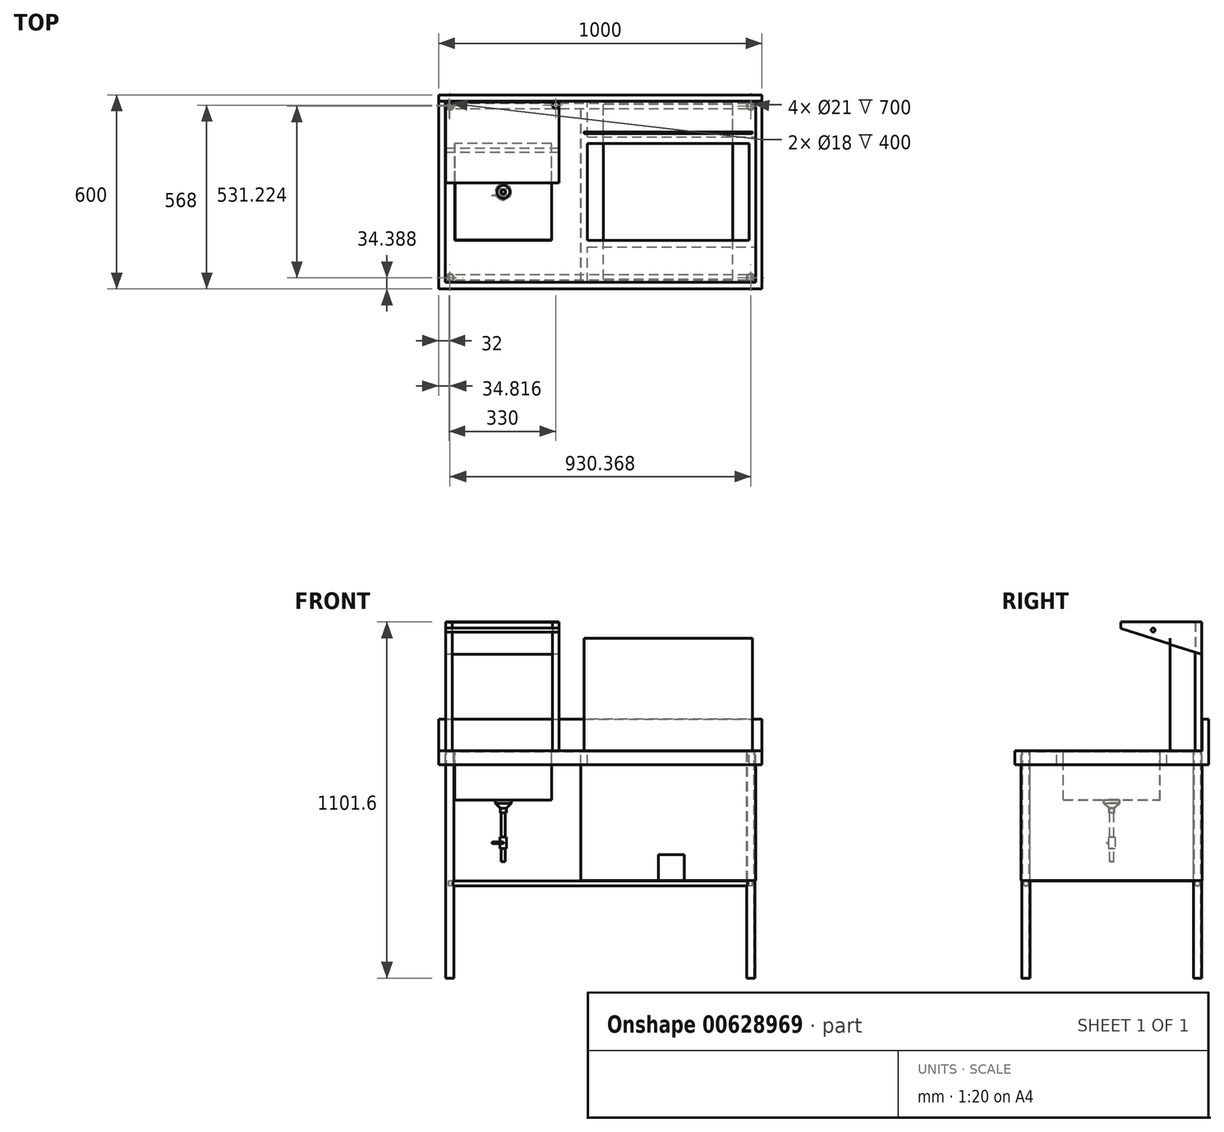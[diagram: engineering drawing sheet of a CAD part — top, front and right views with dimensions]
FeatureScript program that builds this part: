
annotation { "Feature Type Name" : "Feature", "Feature Type Description" : "" }
export const myFeature = defineFeature(function(context is Context, id is Id, definition is map)
    precondition{}
    {
        {
            var Q0;
            Q0=qCreatedBy(makeId("Top.planeOp"),FACE);
            var sketch = newSketch(context, id + "F0", { "sketchPlane" : qUnion([Q0])});
            skPoint(sketch, "E0.middle", {"position": v(230, 0) * mm});
            skLineSegment(sketch, "E1.bottom", {"start": v(500, -300) * mm, "end": v(-500, -300) * mm});
            skLineSegment(sketch, "E1.top", {"start": v(500, 300) * mm, "end": v(-500, 300) * mm});
            skLineSegment(sketch, "E1.left", {"start": v(500, -300) * mm, "end": v(500, 300) * mm});
            skLineSegment(sketch, "E1.right", {"start": v(-500, -300) * mm, "end": v(-500, 300) * mm});
            skPoint(sketch, "E1.middle", {"position": v(0, 0) * mm});
            skSolve(sketch);
        }
        {
            var Q0;
            Q0 = qSketchRegion(id + "F0", true);
            extrude(context, id + "F1", {"entities" : qUnion([Q0]), "oppositeDirection" : true, "depth" : 40 * mm, "offsetDistance" : 25 * mm});
        }
        {
            var Q0;
            Q0=makeQuery(id+"F1.opExtrude","CAP_FACE",FACE,{"disambiguationData":[OSD([sQuery(id+"F0.wireOp",EDGE,"E1.bottom"),sQuery(id+"F0.wireOp",EDGE,"E1.top"),sQuery(id+"F0.wireOp",EDGE,"E1.left"),sQuery(id+"F0.wireOp",EDGE,"E1.right")])],"isStart":false});
            shell(context, id + "F2", {"entities" : qUnion([Q0]), "thickness" : 0.8 * mm});
        }
        {
            var Q0;
            Q0=qCreatedBy(makeId("Top.planeOp"),FACE);
            var sketch = newSketch(context, id + "F3", { "sketchPlane" : qUnion([Q0])});
            skLineSegment(sketch, "E2.bottom", {"start": v(460, -150) * mm, "end": v(-40, -150) * mm});
            skLineSegment(sketch, "E2.top", {"start": v(460, 150) * mm, "end": v(-40, 150) * mm});
            skLineSegment(sketch, "E2.left", {"start": v(460, -150) * mm, "end": v(460, 150) * mm});
            skLineSegment(sketch, "E2.right", {"start": v(-40, -150) * mm, "end": v(-40, 150) * mm});
            skPoint(sketch, "E2.middle", {"position": v(210, 0) * mm});
            skLineSegment(sketch, "E3.bottom", {"start": v(-150, -150) * mm, "end": v(-450, -150) * mm});
            skLineSegment(sketch, "E3.top", {"start": v(-150, 150) * mm, "end": v(-450, 150) * mm});
            skLineSegment(sketch, "E3.left", {"start": v(-150, -150) * mm, "end": v(-150, 150) * mm});
            skLineSegment(sketch, "E3.right", {"start": v(-450, -150) * mm, "end": v(-450, 150) * mm});
            skPoint(sketch, "E3.middle", {"position": v(-300, 0) * mm});
            skPoint(sketch, "E3.middle.positionSnap0", {"position": v(-40, 0) * mm});
            skPoint(sketch, "E3.centerSnap0", {"position": v(-40, 0) * mm});
            skSolve(sketch);
        }
        {
            var Q0;
            Q0 = qSketchRegion(id + "F3", true);
            extrude(context, id + "F4", {"entities" : qUnion([Q0]), "operationType" : NewBodyOperationType.REMOVE, "endBound" : BoundingType.THROUGH_ALL, "oppositeDirection" : true, "depth" : 25 * mm, "offsetDistance" : 25 * mm});
        }
        {
            var Q0;
            Q0=qCreatedBy(makeId("Top.planeOp"),FACE);
            var sketch = newSketch(context, id + "F5", { "sketchPlane" : qUnion([Q0])});
            skLineSegment(sketch, "E4.bottom", {"start": v(-150, -150) * mm, "end": v(-450, -150) * mm});
            skLineSegment(sketch, "E4.top", {"start": v(-150, 150) * mm, "end": v(-450, 150) * mm});
            skLineSegment(sketch, "E4.left", {"start": v(-150, -150) * mm, "end": v(-150, 150) * mm});
            skLineSegment(sketch, "E4.right", {"start": v(-450, -150) * mm, "end": v(-450, 150) * mm});
            skPoint(sketch, "E4.middle", {"position": v(-300, 0) * mm});
            skSolve(sketch);
        }
        {
            var Q0;
            Q0 = qSketchRegion(id + "F5", true);
            extrude(context, id + "F6", {"entities" : qUnion([Q0]), "oppositeDirection" : true, "depth" : 150 * mm, "offsetDistance" : 25 * mm});
        }
        {
            var Q0;
            Q0=makeQuery(id+"F6.opExtrude","CAP_FACE",FACE,{"disambiguationData":[OSD([sQuery(id+"F5.wireOp",EDGE,"E4.bottom"),sQuery(id+"F5.wireOp",EDGE,"E4.top"),sQuery(id+"F5.wireOp",EDGE,"E4.left"),sQuery(id+"F5.wireOp",EDGE,"E4.right")])],"isStart":true});
            shell(context, id + "F7", {"entities" : qUnion([Q0]), "thickness" : 0.8 * mm});
        }
        {
            var Q0;
            Q0=makeQuery(id+"F7.opShell","OFFSET_FACE",FACE,{"disambiguationData":[OSD([sQuery(id+"F5.wireOp",EDGE,"E4.bottom"),sQuery(id+"F5.wireOp",EDGE,"E4.top"),sQuery(id+"F5.wireOp",EDGE,"E4.left"),sQuery(id+"F5.wireOp",EDGE,"E4.right")])]});
            var sketch = newSketch(context, id + "F8", { "sketchPlane" : qUnion([Q0])});
            skPoint(sketch, "E5.center", {"position": v(-300, 0) * mm});
            skCircle(sketch, "E6", {"center": v(-300, 0) * mm, "radius": 20 * mm});
            skSolve(sketch);
        }
        {
            var Q0;
            Q0 = qSketchRegion(id + "F8", true);
            extrude(context, id + "F9", {"entities" : qUnion([Q0]), "operationType" : NewBodyOperationType.REMOVE, "endBound" : BoundingType.UP_TO_NEXT, "oppositeDirection" : true, "depth" : 25 * mm, "offsetDistance" : 25 * mm});
        }
        {
            var Q0;
            Q0=makeQuery(id+"F2.opShell","OFFSET_FACE",FACE,{"disambiguationData":[OSD([sQuery(id+"F0.wireOp",EDGE,"E1.bottom"),sQuery(id+"F0.wireOp",EDGE,"E1.top"),sQuery(id+"F0.wireOp",EDGE,"E1.left"),sQuery(id+"F0.wireOp",EDGE,"E1.right")])]});
            var sketch = newSketch(context, id + "F10", { "sketchPlane" : qUnion([Q0])});
            skLineSegment(sketch, "E7.bottom", {"start": v(500, 300) * mm, "end": v(-500, 300) * mm});
            skLineSegment(sketch, "E7.top", {"start": v(500, -300) * mm, "end": v(-500, -300) * mm});
            skLineSegment(sketch, "E7.left", {"start": v(500, 300) * mm, "end": v(500, -300) * mm});
            skLineSegment(sketch, "E7.right", {"start": v(-500, 300) * mm, "end": v(-500, -300) * mm});
            skPoint(sketch, "E7.middle", {"position": v(0, 0) * mm});
            skLineSegment(sketch, "E8.0", {"start": v(480, 280) * mm, "end": v(-40, 280) * mm});
            skLineSegment(sketch, "E8.1", {"start": v(480, 280) * mm, "end": v(480, 170) * mm});
            skLineSegment(sketch, "E8.2", {"start": v(480, -280) * mm, "end": v(-40, -280) * mm});
            skLineSegment(sketch, "E8.3", {"start": v(-480, 280) * mm, "end": v(-480, -280) * mm});
            skLineSegment(sketch, "E9.left", {"start": v(-40, 280) * mm, "end": v(-40, 170) * mm});
            skLineSegment(sketch, "E9.right", {"start": v(-60, 280) * mm, "end": v(-60, -280) * mm});
            skLineSegment(sketch, "E10.trimOffspring", {"start": v(-60, 280) * mm, "end": v(-480, 280) * mm});
            skLineSegment(sketch, "E11.trimOffspring", {"start": v(-60, -280) * mm, "end": v(-480, -280) * mm});
            skLineSegment(sketch, "E12.bottom", {"start": v(-40, 150) * mm, "end": v(460, 150) * mm});
            skLineSegment(sketch, "E12.top", {"start": v(-40, 170) * mm, "end": v(480, 170) * mm});
            skLineSegment(sketch, "E13.trimOffspring", {"start": v(-40, 150) * mm, "end": v(-40, -150) * mm});
            skLineSegment(sketch, "E14.bottom", {"start": v(-40, -150) * mm, "end": v(460, -150) * mm});
            skLineSegment(sketch, "E14.top", {"start": v(-40, -170) * mm, "end": v(480, -170) * mm});
            skLineSegment(sketch, "E15.trimOffspring", {"start": v(-40, -170) * mm, "end": v(-40, -280) * mm});
            skLineSegment(sketch, "E16.trimOffspring", {"start": v(480, -170) * mm, "end": v(480, -280) * mm});
            skLineSegment(sketch, "E17", {"start": v(460, 150) * mm, "end": v(460, -150) * mm});
            skSolve(sketch);
        }
        {
            var Q0;
            Q0 = qSketchRegion(id + "F10", true);
            extrude(context, id + "F11", {"entities" : qUnion([Q0]), "operationType" : NewBodyOperationType.ADD, "depth" : 40 * mm, "offsetDistance" : 25 * mm});
        }
        {
            var Q0;
            Q0=makeQuery(id+"F11.boolean.opBoolean","SPLIT",FACE,{"disambiguationData":[TD([makeQuery(id+"F4.boolean.opBoolean","COPY",FACE,{"derivedFrom":makeQuery(id+"F4.opExtrude","SWEPT_FACE",FACE,{"disambiguationData":[OSD([sQuery(id+"F3.wireOp",EDGE,"E3.bottom")])]})})])],"derivedFrom":makeQuery(id+"F2.opShell","OFFSET_FACE",FACE,{"disambiguationData":[OSD([sQuery(id+"F0.wireOp",EDGE,"E1.bottom"),sQuery(id+"F0.wireOp",EDGE,"E1.top"),sQuery(id+"F0.wireOp",EDGE,"E1.left"),sQuery(id+"F0.wireOp",EDGE,"E1.right")])]})});
            var sketch = newSketch(context, id + "F12", { "sketchPlane" : qUnion([Q0])});
            skCircle(sketch, "E18", {"center": v(-465.18, 265.61) * mm, "radius": 12.5 * mm});
            skCircle(sketch, "E19.0", {"center": v(-465.18, 265.61) * mm, "radius": 10.5 * mm});
            skLineSegment(sketch, "E20", {"start": v(0, 0) * mm, "end": v(0, 330.65) * mm, "construction": true});
            skLineSegment(sketch, "E21", {"start": v(0, 0) * mm, "end": v(239.47, 0) * mm, "construction": true});
            skLineSegment(sketch, "E22.MirrorCS", {"start": v(0, 0) * mm, "end": v(0, -330.65) * mm, "construction": true});
            skCircle(sketch, "E23.MirrorC", {"center": v(-465.18, -265.61) * mm, "radius": 12.5 * mm});
            skCircle(sketch, "E24.MirrorC", {"center": v(465.18, 265.61) * mm, "radius": 12.5 * mm});
            skCircle(sketch, "E25.MirrorC", {"center": v(465.18, 265.61) * mm, "radius": 10.5 * mm});
            skCircle(sketch, "E26.MirrorC", {"center": v(465.18, -265.61) * mm, "radius": 12.5 * mm});
            skCircle(sketch, "E27.MirrorC", {"center": v(-465.18, -265.61) * mm, "radius": 10.5 * mm});
            skCircle(sketch, "E28.MirrorC", {"center": v(465.18, -265.61) * mm, "radius": 10.5 * mm});
            skSolve(sketch);
        }
        {
            var Q0;
            Q0 = qSketchRegion(id + "F12", true);
            extrude(context, id + "F13", {"entities" : qUnion([Q0]), "operationType" : NewBodyOperationType.ADD, "depth" : 700 * mm, "offsetDistance" : 25 * mm});
        }
        {
            var Q0;
            Q0=qCreatedBy(makeId("Top.planeOp"),FACE);
            cPlane(context, id + "F14", {"entities" : qUnion([Q0]), "cplaneType" : CPlaneType.OFFSET, "offset" : 1.2 * mm, "width" : 150 * mm, "height" : 150 * mm});
        }
        {
            var Q0;
            Q0=qCreatedBy(makeId("Top.planeOp"),FACE);
            cPlane(context, id + "F15", {"entities" : qUnion([Q0]), "cplaneType" : CPlaneType.OFFSET, "offset" : 400 * mm, "oppositeDirection" : true, "width" : 150 * mm, "height" : 150 * mm});
        }
        {
            var Q0;
            Q0=qCreatedBy(makeId("Right.planeOp"),FACE);
            var sketch = newSketch(context, id + "F16", { "sketchPlane" : qUnion([Q0])});
            skCircle(sketch, "E29", {"center": v(265, -408) * mm, "radius": 8 * mm});
            skCircle(sketch, "E30", {"center": v(-265, -408) * mm, "radius": 8 * mm});
            skSolve(sketch);
        }
        {
            var Q0;
            Q0 = qSketchRegion(id + "F16", true);
            extrude(context, id + "F17", {"entities" : qUnion([Q0]), "operationType" : NewBodyOperationType.ADD, "depth" : 940 * mm, "offsetDistance" : 25 * mm, "symmetric" : true});
        }
        {
            var Q0;
            Q0=qCreatedBy(id+"F15.planeOp",FACE);
            var sketch = newSketch(context, id + "F18", { "sketchPlane" : qUnion([Q0])});
            skLineSegment(sketch, "E31.bottom", {"start": v(410, -270) * mm, "end": v(10, -270) * mm});
            skLineSegment(sketch, "E31.top", {"start": v(410, 270) * mm, "end": v(10, 270) * mm});
            skLineSegment(sketch, "E31.left", {"start": v(410, -270) * mm, "end": v(410, 270) * mm});
            skLineSegment(sketch, "E31.right", {"start": v(10, -270) * mm, "end": v(10, 270) * mm});
            skPoint(sketch, "E31.middle", {"position": v(210, 0) * mm});
            skSolve(sketch);
        }
        {
            var Q0;
            Q0 = qSketchRegion(id + "F18", true);
            extrude(context, id + "F19", {"entities" : qUnion([Q0]), "operationType" : NewBodyOperationType.ADD, "depth" : 1 * mm, "offsetDistance" : 25 * mm});
        }
        {
            var Q0;
            Q0=makeQuery(id+"F1.opExtrude","CAP_FACE",FACE,{"disambiguationData":[OSD([sQuery(id+"F0.wireOp",EDGE,"E1.bottom"),sQuery(id+"F0.wireOp",EDGE,"E1.top"),sQuery(id+"F0.wireOp",EDGE,"E1.left"),sQuery(id+"F0.wireOp",EDGE,"E1.right")])],"isStart":true});
            var sketch = newSketch(context, id + "F20", { "sketchPlane" : qUnion([Q0])});
            skLineSegment(sketch, "E32.bottom", {"start": v(-50, 181) * mm, "end": v(470, 181) * mm});
            skLineSegment(sketch, "E32.top", {"start": v(-50, 180) * mm, "end": v(470, 180) * mm});
            skLineSegment(sketch, "E32.left", {"start": v(-50, 181) * mm, "end": v(-50, 180) * mm});
            skLineSegment(sketch, "E32.right", {"start": v(470, 181) * mm, "end": v(470, 180) * mm});
            skSolve(sketch);
        }
        {
            var Q0;
            Q0 = qSketchRegion(id + "F20", true);
            extrude(context, id + "F21", {"entities" : qUnion([Q0]), "operationType" : NewBodyOperationType.ADD, "depth" : 350 * mm, "offsetDistance" : 25 * mm});
        }
        {
            var Q0;
            Q0=makeQuery(id+"F21.opExtrude","SWEPT_FACE",FACE,{"disambiguationData":[OSD([sQuery(id+"F20.wireOp",EDGE,"E32.right")])]});
            var sketch = newSketch(context, id + "F22", { "sketchPlane" : qUnion([Q0])});
            skCircle(sketch, "E33", {"center": v(183.5, 2.5) * mm, "radius": 2.5 * mm});
            skSolve(sketch);
        }
        {
            var Q0;
            Q0 = qSketchRegion(id + "F22", true);
            var Q1;
            Q1=makeQuery(id+"F21.opExtrude","SWEPT_FACE",FACE,{"disambiguationData":[OSD([sQuery(id+"F20.wireOp",EDGE,"E32.left")])]});
            extrude(context, id + "F23", {"entities" : qUnion([Q0]), "operationType" : NewBodyOperationType.ADD, "endBound" : BoundingType.UP_TO_SURFACE, "oppositeDirection" : true, "depth" : 500 * mm, "endBoundEntityFace" : qUnion([Q1]), "offsetDistance" : 25 * mm});
        }
        {
            var Q0;
            Q0=makeQuery(id+"F11.opExtrude","CAP_FACE",FACE,{"disambiguationData":[OSD([sQuery(id+"F10.wireOp",EDGE,"E7.bottom"),sQuery(id+"F10.wireOp",EDGE,"E7.top"),sQuery(id+"F10.wireOp",EDGE,"E7.left"),sQuery(id+"F10.wireOp",EDGE,"E7.right"),sQuery(id+"F10.wireOp",EDGE,"E8.0"),sQuery(id+"F10.wireOp",EDGE,"E8.1"),sQuery(id+"F10.wireOp",EDGE,"E8.2"),sQuery(id+"F10.wireOp",EDGE,"E8.3"),sQuery(id+"F10.wireOp",EDGE,"E9.left"),sQuery(id+"F10.wireOp",EDGE,"E9.right"),sQuery(id+"F10.wireOp",EDGE,"E10.trimOffspring"),sQuery(id+"F10.wireOp",EDGE,"E11.trimOffspring"),sQuery(id+"F10.wireOp",EDGE,"E12.bottom"),sQuery(id+"F10.wireOp",EDGE,"E12.top"),sQuery(id+"F10.wireOp",EDGE,"E13.trimOffspring"),sQuery(id+"F10.wireOp",EDGE,"192a2169-85b4-4757-ab78-00c488c10352.trimOffspring"),sQuery(id+"F10.wireOp",EDGE,"E14.bottom"),sQuery(id+"F10.wireOp",EDGE,"E14.top"),sQuery(id+"F10.wireOp",EDGE,"E15.trimOffspring"),sQuery(id+"F10.wireOp",EDGE,"E16.trimOffspring")])],"isStart":false});
            var sketch = newSketch(context, id + "F24", { "sketchPlane" : qUnion([Q0])});
            skLineSegment(sketch, "E34.bottom", {"start": v(-60, 280) * mm, "end": v(480, 280) * mm});
            skLineSegment(sketch, "E34.top", {"start": v(-60, -280) * mm, "end": v(480, -280) * mm});
            skLineSegment(sketch, "E34.left", {"start": v(-60, 280) * mm, "end": v(-60, -280) * mm});
            skLineSegment(sketch, "E34.right", {"start": v(480, 280) * mm, "end": v(480, -280) * mm});
            skSolve(sketch);
        }
        {
            var Q0;
            Q0 = qSketchRegion(id + "F24", true);
            var Q1;
            Q1=makeQuery(id+"F19.opExtrude","CAP_FACE",FACE,{"disambiguationData":[OSD([sQuery(id+"F18.wireOp",EDGE,"E31.bottom"),sQuery(id+"F18.wireOp",EDGE,"E31.top"),sQuery(id+"F18.wireOp",EDGE,"E31.left"),sQuery(id+"F18.wireOp",EDGE,"E31.right")])],"isStart":false});
            extrude(context, id + "F25", {"entities" : qUnion([Q0]), "endBound" : BoundingType.UP_TO_SURFACE, "depth" : 25 * mm, "endBoundEntityFace" : qUnion([Q1]), "offsetDistance" : 25 * mm});
        }
        {
            var Q0;
            Q0=makeQuery(id+"F25.opExtrude","CAP_FACE",FACE,{"disambiguationData":[OSD([sQuery(id+"F24.wireOp",EDGE,"E34.bottom"),sQuery(id+"F24.wireOp",EDGE,"E34.top"),sQuery(id+"F24.wireOp",EDGE,"E34.left"),sQuery(id+"F24.wireOp",EDGE,"E34.right")])],"isStart":true});
            var Q1;
            Q1=makeQuery(id+"F25.opExtrude","CAP_FACE",FACE,{"disambiguationData":[OSD([sQuery(id+"F24.wireOp",EDGE,"E34.bottom"),sQuery(id+"F24.wireOp",EDGE,"E34.top"),sQuery(id+"F24.wireOp",EDGE,"E34.left"),sQuery(id+"F24.wireOp",EDGE,"E34.right")])],"isStart":false});
            shell(context, id + "F26", {"entities" : qUnion([Q0, Q1]), "thickness" : 0.8 * mm});
        }
        {
            var Q0;
            Q0=makeQuery(id+"F25.opExtrude","SWEPT_FACE",FACE,{"disambiguationData":[OSD([sQuery(id+"F24.wireOp",EDGE,"E34.bottom")])]});
            var sketch = newSketch(context, id + "F27", { "sketchPlane" : qUnion([Q0])});
            skLineSegment(sketch, "E35.bottom", {"start": v(180, -399) * mm, "end": v(260, -399) * mm});
            skLineSegment(sketch, "E35.top", {"start": v(180, -319) * mm, "end": v(260, -319) * mm});
            skLineSegment(sketch, "E35.left", {"start": v(180, -399) * mm, "end": v(180, -319) * mm});
            skLineSegment(sketch, "E35.right", {"start": v(260, -399) * mm, "end": v(260, -319) * mm});
            skSolve(sketch);
        }
        {
            var Q0;
            Q0 = qSketchRegion(id + "F27", true);
            extrude(context, id + "F28", {"entities" : qUnion([Q0]), "operationType" : NewBodyOperationType.REMOVE, "oppositeDirection" : true, "depth" : 25 * mm, "offsetDistance" : 25 * mm});
        }
        {
            var Q0;
            Q0=qCreatedBy(makeId("Front.planeOp"),FACE);
            var sketch = newSketch(context, id + "F29", { "sketchPlane" : qUnion([Q0])});
            skLineSegment(sketch, "E36", {"start": v(-300, -110.82) * mm, "end": v(-300, -187.74) * mm, "construction": true});
            skLineSegment(sketch, "E37", {"start": v(-325, -150) * mm, "end": v(-325, -160) * mm});
            skLineSegment(sketch, "E38", {"start": v(-325, -160) * mm, "end": v(-309.25, -175.75) * mm});
            skLineSegment(sketch, "E39", {"start": v(-309.25, -175.75) * mm, "end": v(-309.25, -190) * mm});
            skLineSegment(sketch, "E40", {"start": v(-325, -150) * mm, "end": v(-300, -150) * mm});
            skLineSegment(sketch, "E41", {"start": v(-309.25, -190) * mm, "end": v(-300, -190) * mm});
            skLineSegment(sketch, "E42", {"start": v(-300, -150) * mm, "end": v(-300, -190) * mm});
            skSolve(sketch);
        }
        {
            var Q0;
            Q0 = qSketchRegion(id + "F29", true);
            var Q1;
            Q1=sQuery(id+"F29.wireOp",EDGE,"E36");
            revolve(context, id + "F30", {"operationType" : NewBodyOperationType.ADD, "entities" : qUnion([Q0]), "axis" : qUnion([Q1]), "revolveType" : RevolveType.FULL});
        }
        {
            var Q0;
            Q0=makeQuery(id+"F30.opRevolve","SWEPT_FACE",FACE,{"disambiguationData":[OSD([sQuery(id+"F29.wireOp",EDGE,"E41")])]});
            var Q1;
            Q1=makeQuery(id+"F30.opRevolve","SWEPT_FACE",FACE,{"disambiguationData":[OSD([sQuery(id+"F29.wireOp",EDGE,"E40")])]});
            shell(context, id + "F31", {"entities" : qUnion([Q0, Q1]), "thickness" : 2.5 * mm});
        }
        {
            var Q0;
            Q0=makeQuery(id+"F1.opExtrude","CAP_FACE",FACE,{"disambiguationData":[OSD([sQuery(id+"F0.wireOp",EDGE,"E1.bottom"),sQuery(id+"F0.wireOp",EDGE,"E1.top"),sQuery(id+"F0.wireOp",EDGE,"E1.left"),sQuery(id+"F0.wireOp",EDGE,"E1.right")])],"isStart":true});
            var sketch = newSketch(context, id + "F32", { "sketchPlane" : qUnion([Q0])});
            skLineSegment(sketch, "E43.top", {"start": v(500, -300) * mm, "end": v(-500, -300) * mm});
            skLineSegment(sketch, "E43.left", {"start": v(500, 280) * mm, "end": v(500, -300) * mm});
            skLineSegment(sketch, "E43.right", {"start": v(-500, 280) * mm, "end": v(-500, -300) * mm});
            skPoint(sketch, "E43.middle", {"position": v(0, 0) * mm});
            skLineSegment(sketch, "E44.0", {"start": v(480, -280) * mm, "end": v(480, 280) * mm});
            skLineSegment(sketch, "E44.1", {"start": v(-480, -280) * mm, "end": v(480, -280) * mm});
            skLineSegment(sketch, "E44.2", {"start": v(-480, 280) * mm, "end": v(-480, -280) * mm});
            skLineSegment(sketch, "E44.3", {"start": v(500, 280) * mm, "end": v(480, 280) * mm});
            skLineSegment(sketch, "E45.trimOffspring", {"start": v(-480, 280) * mm, "end": v(-500, 280) * mm});
            skSolve(sketch);
        }
        {
            var Q0;
            Q0 = qSketchRegion(id + "F32", true);
            extrude(context, id + "F33", {"entities" : qUnion([Q0]), "depth" : 2 * mm, "offsetDistance" : 25 * mm});
        }
        {
            var Q0;
            Q0=makeQuery(id+"F1.opExtrude","CAP_FACE",FACE,{"disambiguationData":[OSD([sQuery(id+"F0.wireOp",EDGE,"E1.bottom"),sQuery(id+"F0.wireOp",EDGE,"E1.top"),sQuery(id+"F0.wireOp",EDGE,"E1.left"),sQuery(id+"F0.wireOp",EDGE,"E1.right")])],"isStart":true});
            var sketch = newSketch(context, id + "F34", { "sketchPlane" : qUnion([Q0])});
            skLineSegment(sketch, "E46.bottom", {"start": v(-500, 300) * mm, "end": v(500, 300) * mm});
            skLineSegment(sketch, "E46.top", {"start": v(-500, 280) * mm, "end": v(500, 280) * mm});
            skLineSegment(sketch, "E46.left", {"start": v(-500, 300) * mm, "end": v(-500, 280) * mm});
            skLineSegment(sketch, "E46.right", {"start": v(500, 300) * mm, "end": v(500, 280) * mm});
            skSolve(sketch);
        }
        {
            var Q0;
            Q0 = qSketchRegion(id + "F34", true);
            extrude(context, id + "F35", {"entities" : qUnion([Q0]), "operationType" : NewBodyOperationType.ADD, "depth" : 100 * mm, "offsetDistance" : 25 * mm});
        }
        {
            var Q0;
            Q0=qCreatedBy(makeId("Front.planeOp"),FACE);
            var sketch = newSketch(context, id + "F36", { "sketchPlane" : qUnion([Q0])});
            skLineSegment(sketch, "E47.bottom", {"start": v(-300, -190) * mm, "end": v(-306.35, -190) * mm});
            skLineSegment(sketch, "E47.top", {"start": v(-300, -340) * mm, "end": v(-306.35, -340) * mm});
            skLineSegment(sketch, "E47.left", {"start": v(-300, -190) * mm, "end": v(-300, -340) * mm});
            skLineSegment(sketch, "E47.right", {"start": v(-306.35, -190) * mm, "end": v(-306.35, -340) * mm});
            skSolve(sketch);
        }
        {
            var Q0;
            Q0=makeQuery(id+"F36.imprint","IMPRINT",FACE,{"disambiguationData":[TD([[makeQuery(id+"F36.imprint","IMPRINT",EDGE,{"derivedFrom":sQuery(id+"F36.wireOp",EDGE,"E47.bottom")}),1.0]])]});
            var Q1;
            Q1=sQuery(id+"F36.wireOp",EDGE,"E47.left");
            revolve(context, id + "F37", {"operationType" : NewBodyOperationType.ADD, "entities" : qUnion([Q0]), "axis" : qUnion([Q1]), "revolveType" : RevolveType.FULL});
        }
        {
            var Q0;
            Q0=qCreatedBy(makeId("Front.planeOp"),FACE);
            var sketch = newSketch(context, id + "F38", { "sketchPlane" : qUnion([Q0])});
            skLineSegment(sketch, "E48.bottom", {"start": v(-310.18, -265) * mm, "end": v(-290.18, -265) * mm});
            skLineSegment(sketch, "E48.top", {"start": v(-310.18, -300) * mm, "end": v(-290.18, -300) * mm});
            skLineSegment(sketch, "E48.left", {"start": v(-310.18, -265) * mm, "end": v(-310.18, -300) * mm});
            skLineSegment(sketch, "E48.right", {"start": v(-290.18, -265) * mm, "end": v(-290.18, -300) * mm});
            skSolve(sketch);
        }
        {
            var Q0;
            Q0 = qSketchRegion(id + "F38", true);
            extrude(context, id + "F39", {"entities" : qUnion([Q0]), "operationType" : NewBodyOperationType.ADD, "depth" : 20 * mm, "offsetDistance" : 25 * mm, "symmetric" : true});
        }
        {
            var Q0;
            Q0=makeQuery(id+"F39.opExtrude","CAP_FACE",FACE,{"disambiguationData":[OSD([sQuery(id+"F38.wireOp",EDGE,"E48.bottom"),sQuery(id+"F38.wireOp",EDGE,"E48.top"),sQuery(id+"F38.wireOp",EDGE,"E48.left"),sQuery(id+"F38.wireOp",EDGE,"E48.right")])],"isStart":false});
            var sketch = newSketch(context, id + "F40", { "sketchPlane" : qUnion([Q0])});
            skLineSegment(sketch, "E49.bottom", {"start": v(-300.18, -285) * mm, "end": v(-332.52, -285) * mm});
            skLineSegment(sketch, "E49.top", {"start": v(-300.18, -280) * mm, "end": v(-332.52, -280) * mm});
            skLineSegment(sketch, "E49.left", {"start": v(-300.18, -285) * mm, "end": v(-300.18, -280) * mm});
            skLineSegment(sketch, "E49.right", {"start": v(-334.52, -283) * mm, "end": v(-334.52, -282) * mm});
            skPoint(sketch, "E49.middle", {"position": v(-317.35, -282.5) * mm});
            skPoint(sketch, "E49.centerSnap0", {"position": v(-310.18, -282.5) * mm});
            skPoint(sketch, "E50.visualSharp", {"position": v(-334.52, -280) * mm});
            skArc(sketch, "E50.filletArc", {"start": v(-332.52, -280) * mm, "mid": v(-333.94, -280.59) * mm, "end": v(-334.52, -282) * mm});
            skPoint(sketch, "E51.visualSharp", {"position": v(-334.52, -285) * mm});
            skArc(sketch, "E51.filletArc", {"start": v(-334.52, -283) * mm, "mid": v(-333.94, -284.41) * mm, "end": v(-332.52, -285) * mm});
            skSolve(sketch);
        }
        {
            var Q0;
            Q0 = qSketchRegion(id + "F40", true);
            extrude(context, id + "F41", {"entities" : qUnion([Q0]), "operationType" : NewBodyOperationType.ADD, "depth" : 3 * mm, "offsetDistance" : 25 * mm});
        }
        {
            var Q0;
            Q0=makeQuery(id+"F39.opExtrude","CAP_FACE",FACE,{"disambiguationData":[OSD([sQuery(id+"F38.wireOp",EDGE,"E48.bottom"),sQuery(id+"F38.wireOp",EDGE,"E48.top"),sQuery(id+"F38.wireOp",EDGE,"E48.left"),sQuery(id+"F38.wireOp",EDGE,"E48.right")])],"isStart":false});
            var sketch = newSketch(context, id + "F42", { "sketchPlane" : qUnion([Q0])});
            skCircle(sketch, "E52", {"center": v(-300.18, -282.5) * mm, "radius": 1.5 * mm});
            skSolve(sketch);
        }
        {
            var Q0;
            Q0 = qSketchRegion(id + "F42", true);
            extrude(context, id + "F43", {"entities" : qUnion([Q0]), "operationType" : NewBodyOperationType.ADD, "depth" : 5 * mm, "offsetDistance" : 25 * mm});
        }
        {
            var Q0;
            Q0=makeQuery(id+"F1.opExtrude","CAP_FACE",FACE,{"disambiguationData":[OSD([sQuery(id+"F0.wireOp",EDGE,"E1.bottom"),sQuery(id+"F0.wireOp",EDGE,"E1.top"),sQuery(id+"F0.wireOp",EDGE,"E1.left"),sQuery(id+"F0.wireOp",EDGE,"E1.right")])],"isStart":true});
            var sketch = newSketch(context, id + "F44", { "sketchPlane" : qUnion([Q0])});
            skCircle(sketch, "E53", {"center": v(-468, 268) * mm, "radius": 10 * mm});
            skCircle(sketch, "E54", {"center": v(-138, 268) * mm, "radius": 10 * mm});
            skCircle(sketch, "E55.0", {"center": v(-468, 268) * mm, "radius": 9 * mm});
            skCircle(sketch, "E56.0", {"center": v(-138, 268) * mm, "radius": 9 * mm});
            skSolve(sketch);
        }
        {
            var Q0;
            Q0 = qSketchRegion(id + "F44", true);
            extrude(context, id + "F45", {"entities" : qUnion([Q0]), "operationType" : NewBodyOperationType.ADD, "depth" : 400 * mm, "offsetDistance" : 25 * mm});
        }
        {
            var Q0;
            Q0=makeQuery(id+"F45.opExtrude","CAP_FACE",FACE,{"disambiguationData":[OSD([sQuery(id+"F44.wireOp",EDGE,"E53"),sQuery(id+"F44.wireOp",EDGE,"E55.0")])],"isStart":false});
            var sketch = newSketch(context, id + "F46", { "sketchPlane" : qUnion([Q0])});
            skLineSegment(sketch, "E57.bottom", {"start": v(-478, 278) * mm, "end": v(-128, 278) * mm});
            skLineSegment(sketch, "E57.top", {"start": v(-478, 28) * mm, "end": v(-128, 28) * mm});
            skLineSegment(sketch, "E57.left", {"start": v(-478, 278) * mm, "end": v(-478, 28) * mm});
            skLineSegment(sketch, "E57.right", {"start": v(-128, 278) * mm, "end": v(-128, 28) * mm});
            skSolve(sketch);
        }
        {
            var Q0;
            Q0 = qSketchRegion(id + "F46", true);
            extrude(context, id + "F47", {"entities" : qUnion([Q0]), "operationType" : NewBodyOperationType.ADD, "depth" : 0.8 * mm, "offsetDistance" : 25 * mm});
        }
        {
            var Q0;
            Q0=makeQuery(id+"F47.opExtrude","SWEPT_FACE",FACE,{"disambiguationData":[OSD([sQuery(id+"F46.wireOp",EDGE,"E57.left")])]});
            var sketch = newSketch(context, id + "F48", { "sketchPlane" : qUnion([Q0])});
            skLineSegment(sketch, "E58", {"start": v(-278, 400.8) * mm, "end": v(-28, 400.8) * mm});
            skLineSegment(sketch, "E59", {"start": v(-28, 400.8) * mm, "end": v(-28, 380.8) * mm});
            skLineSegment(sketch, "E60", {"start": v(-28, 380.8) * mm, "end": v(-278, 300.8) * mm});
            skLineSegment(sketch, "E61", {"start": v(-278, 300.8) * mm, "end": v(-278, 400.8) * mm});
            skCircle(sketch, "E62", {"center": v(-128, 375.8) * mm, "radius": 6 * mm});
            skSolve(sketch);
        }
        {
            var Q0;
            Q0 = qSketchRegion(id + "F48", true);
            extrude(context, id + "F49", {"entities" : qUnion([Q0]), "depth" : 0.8 * mm, "offsetDistance" : 25 * mm});
        }
        {
            var Q0;
            Q0=makeQuery(id+"F47.opExtrude","SWEPT_FACE",FACE,{"disambiguationData":[OSD([sQuery(id+"F46.wireOp",EDGE,"E57.right")])]});
            var sketch = newSketch(context, id + "F50", { "sketchPlane" : qUnion([Q0])});
            skLineSegment(sketch, "E63", {"start": v(28, 400.8) * mm, "end": v(278, 400.8) * mm});
            skLineSegment(sketch, "E64", {"start": v(278, 400.8) * mm, "end": v(278, 300.8) * mm});
            skLineSegment(sketch, "E65", {"start": v(278, 300.8) * mm, "end": v(28, 380.8) * mm});
            skLineSegment(sketch, "E66", {"start": v(28, 380.8) * mm, "end": v(28, 400.8) * mm});
            skCircle(sketch, "E67", {"center": v(128, 375.8) * mm, "radius": 6 * mm});
            skSolve(sketch);
        }
        {
            var Q0;
            Q0 = qSketchRegion(id + "F50", true);
            extrude(context, id + "F51", {"entities" : qUnion([Q0]), "depth" : 0.8 * mm, "offsetDistance" : 25 * mm});
        }
        {
            var Q0;
            Q0=makeQuery(id+"F51.opExtrude","SWEPT_FACE",FACE,{"disambiguationData":[OSD([sQuery(id+"F50.wireOp",EDGE,"E64")])]});
            var sketch = newSketch(context, id + "F52", { "sketchPlane" : qUnion([Q0])});
            skLineSegment(sketch, "E68.bottom", {"start": v(127.2, 400.8) * mm, "end": v(478.8, 400.8) * mm});
            skLineSegment(sketch, "E68.top", {"start": v(127.2, 300.8) * mm, "end": v(478.8, 300.8) * mm});
            skLineSegment(sketch, "E68.left", {"start": v(127.2, 400.8) * mm, "end": v(127.2, 300.8) * mm});
            skLineSegment(sketch, "E68.right", {"start": v(478.8, 400.8) * mm, "end": v(478.8, 300.8) * mm});
            skSolve(sketch);
        }
        {
            var Q0;
            Q0 = qSketchRegion(id + "F52", true);
            extrude(context, id + "F53", {"entities" : qUnion([Q0]), "depth" : 0.8 * mm, "offsetDistance" : 25 * mm});
        }
        {
            var Q0;
            Q0=makeQuery(id+"F49.opExtrude","CAP_FACE",FACE,{"disambiguationData":[OSD([sQuery(id+"F48.wireOp",EDGE,"E58"),sQuery(id+"F48.wireOp",EDGE,"E59"),sQuery(id+"F48.wireOp",EDGE,"E60"),sQuery(id+"F48.wireOp",EDGE,"E61"),sQuery(id+"F48.wireOp",EDGE,"E62")])],"isStart":false});
            var sketch = newSketch(context, id + "F54", { "sketchPlane" : qUnion([Q0])});
            skCircle(sketch, "E69", {"center": v(-128, 375.8) * mm, "radius": 6 * mm});
            skSolve(sketch);
        }
        {
            var Q0;
            Q0 = qSketchRegion(id + "F54", true);
            var Q1;
            Q1=makeQuery(id+"F51.opExtrude","CAP_FACE",FACE,{"disambiguationData":[OSD([sQuery(id+"F50.wireOp",EDGE,"E63"),sQuery(id+"F50.wireOp",EDGE,"E64"),sQuery(id+"F50.wireOp",EDGE,"E65"),sQuery(id+"F50.wireOp",EDGE,"E66"),sQuery(id+"F50.wireOp",EDGE,"E67")])],"isStart":false});
            extrude(context, id + "F55", {"entities" : qUnion([Q0]), "endBound" : BoundingType.UP_TO_SURFACE, "oppositeDirection" : true, "depth" : 25 * mm, "endBoundEntityFace" : qUnion([Q1]), "offsetDistance" : 25 * mm});
        }
    });
